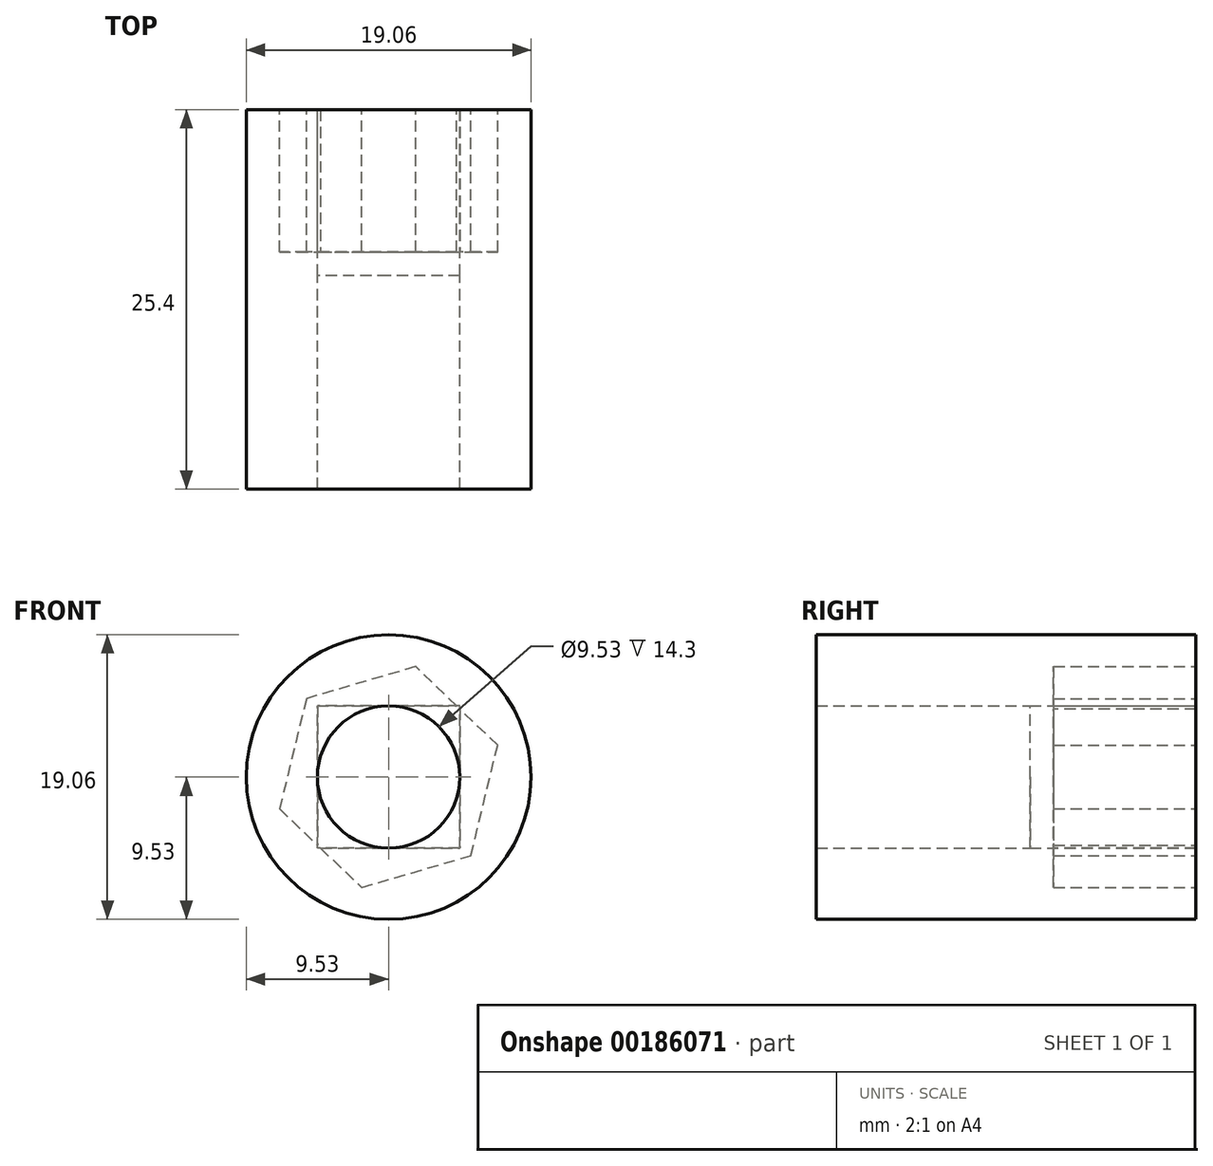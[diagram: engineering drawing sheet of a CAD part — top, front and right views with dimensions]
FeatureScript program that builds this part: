
annotation { "Feature Type Name" : "Feature", "Feature Type Description" : "" }
export const myFeature = defineFeature(function(context is Context, id is Id, definition is map)
    precondition{}
    {
        {
            var Q0;
            Q0=qCreatedBy(makeId("Front.planeOp"),FACE);
            var sketch = newSketch(context, id + "F0", { "sketchPlane" : qUnion([Q0])});
            skCircle(sketch, "E0", {"center": v(0, 0) * mm, "radius": 9.53 * mm});
            skSolve(sketch);
        }
        {
            var Q0;
            Q0 = qSketchRegion(id + "F0", true);
            extrude(context, id + "F1", {"entities" : qUnion([Q0]), "depth" : 25.4 * mm});
        }
        {
            var Q0;
            Q0=qCreatedBy(makeId("Front.planeOp"),FACE);
            var sketch = newSketch(context, id + "F2", { "sketchPlane" : qUnion([Q0])});
            skLineSegment(sketch, "E1.bottom", {"start": v(4.76, -4.76) * mm, "end": v(-4.76, -4.76) * mm});
            skLineSegment(sketch, "E1.top", {"start": v(4.76, 4.76) * mm, "end": v(-4.76, 4.76) * mm});
            skLineSegment(sketch, "E1.left", {"start": v(4.76, -4.76) * mm, "end": v(4.76, 4.76) * mm});
            skLineSegment(sketch, "E1.right", {"start": v(-4.76, -4.76) * mm, "end": v(-4.76, 4.76) * mm});
            skPoint(sketch, "E1.middle", {"position": v(0, 0) * mm});
            skSolve(sketch);
        }
        {
            var Q0;
            Q0=qCreatedBy(makeId("Front.planeOp"),FACE);
            var sketch = newSketch(context, id + "F3", { "sketchPlane" : qUnion([Q0])});
            skCircle(sketch, "E2", {"center": v(0, 0) * mm, "radius": 4.76 * mm});
            skSolve(sketch);
        }
        {
            var Q0;
            Q0=makeQuery(id+"F3.imprint","IMPRINT",FACE,{"disambiguationData":[TD([[makeQuery(id+"F3.imprint","IMPRINT",EDGE,{"derivedFrom":sQuery(id+"F3.wireOp",EDGE,"E2")}),1.0]])]});
            extrude(context, id + "F4", {"entities" : qUnion([Q0]), "operationType" : NewBodyOperationType.REMOVE, "endBound" : BoundingType.THROUGH_ALL, "depth" : 25.4 * mm});
        }
        {
            var Q0;
            Q0 = qSketchRegion(id + "F2", true);
            extrude(context, id + "F5", {"entities" : qUnion([Q0]), "operationType" : NewBodyOperationType.REMOVE, "depth" : 11.1 * mm});
        }
        {
            var Q0;
            Q0=makeQuery(id+"F1.opExtrude","CAP_FACE",FACE,{"disambiguationData":[OSD([sQuery(id+"F0.wireOp",EDGE,"E0")])],"isStart":true});
            var sketch = newSketch(context, id + "F6", { "sketchPlane" : qUnion([Q0])});
            skCircle(sketch, "E3.cCircle", {"center": v(0, 0) * mm, "radius": 6.59 * mm, "construction": true});
            skLineSegment(sketch, "E3.0", {"start": v(-7.3, 2.13) * mm, "end": v(-1.8, 7.4) * mm});
            skLineSegment(sketch, "E3.1", {"start": v(-1.8, 7.4) * mm, "end": v(5.5, 5.26) * mm});
            skLineSegment(sketch, "E3.2", {"start": v(5.5, 5.26) * mm, "end": v(7.3, -2.13) * mm});
            skLineSegment(sketch, "E3.3", {"start": v(7.3, -2.13) * mm, "end": v(1.8, -7.4) * mm});
            skLineSegment(sketch, "E3.4", {"start": v(1.8, -7.4) * mm, "end": v(-5.5, -5.26) * mm});
            skLineSegment(sketch, "E3.5", {"start": v(-5.5, -5.26) * mm, "end": v(-7.3, 2.13) * mm});
            skPoint(sketch, "E3.0.midPoint", {"position": v(-4.55, 4.76) * mm});
            skSolve(sketch);
        }
        {
            var Q0;
            Q0 = qSketchRegion(id + "F6", true);
            extrude(context, id + "F7", {"entities" : qUnion([Q0]), "operationType" : NewBodyOperationType.REMOVE, "oppositeDirection" : true, "depth" : 9.52 * mm});
        }
    });
